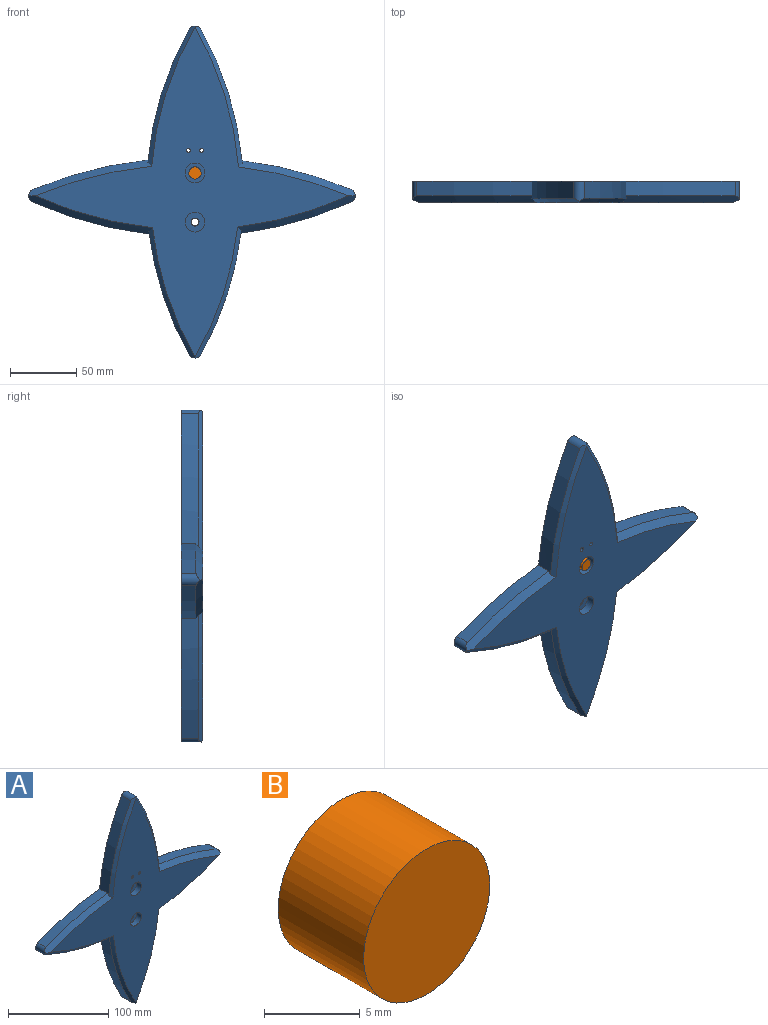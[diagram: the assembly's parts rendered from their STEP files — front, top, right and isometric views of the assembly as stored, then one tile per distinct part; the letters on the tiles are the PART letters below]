
ASSEMBLY  parts=2 mates=1
PART A: 30 faces, bbox 248.6x16x252.7 mm
  f0: cylinder r=3mm len=9.5mm, axis (0,1,0), area 179.1mm2, adj f10,f12
  f1: cylinder r=289.43mm len=87.94mm, axis (0,1,0), area 1007.8mm2, adj f2,f10,f18,f25
  f2: cylinder r=250mm len=92.9mm, axis (0,1,0), area 1254mm2, adj f1,f10,f18,f21,f23
  f3: cylinder r=250mm len=93.46mm, axis (0,1,0), area 1261.3mm2, adj f4,f10,f15,f22,f23
  f4: cylinder r=289.43mm len=83.32mm, axis (0,1,0), area 956.6mm2, adj f3,f10,f15,f26
  f5: cylinder r=310.23mm len=82.35mm, axis (0,1,0), area 940.1mm2, adj f6,f10,f16,f26
  f6: cylinder r=250mm len=100.98mm, axis (0,1,0), area 1359.7mm2, adj f5,f10,f16,f20,f24
  f7: cylinder r=250mm len=100.45mm, axis (0,1,0), area 1352.8mm2, adj f8,f10,f17,f19,f24
  f8: cylinder r=310.23mm len=86.95mm, axis (0,1,0), area 991.1mm2, adj f7,f10,f17,f25
  f9: plane 248.27x236.06mm, normal (0,-1,0), area 15523.8mm2, adj f11,f13,f15,f16,f17,f18,f19,f20
  f10: plane 250.21x246.06mm, normal (0,1,0), area 18914.9mm2, adj f0,f1,f2,f3,f4,f5,f6,f7
  f11: cylinder r=7.5mm len=15mm, axis (0,-1,0), area 306.3mm2, adj f9,f12
  f12: plane 15x15mm, normal (0,-1,0), area 148.4mm2, adj f0,f11
  f13: cylinder r=7.5mm len=15mm, axis (0,-1,0), area 306.3mm2, adj f9,f14
  f14: plane 15x15mm, normal (0,-1,0), area 146.5mm2, adj f13,f29
  f15: cone r=284.43mm half-angle=45deg, axis (0,1,0), area 632.2mm2, adj f3,f4,f9,f16,f22,f26
  f16: cone r=305.23mm half-angle=45deg, axis (0,1,0), area 622.6mm2, adj f5,f6,f9,f15,f20,f26
  f17: cone r=305.23mm half-angle=45deg, axis (0,1,0), area 655.4mm2, adj f7,f8,f9,f18,f19,f25
  f18: cone r=284.43mm half-angle=45deg, axis (0,1,0), area 665.1mm2, adj f1,f2,f9,f17,f21,f25
  f19: cone r=247mm half-angle=45deg, axis (0,1,0), area 465.8mm2, adj f7,f9,f17,f20,f24
  f20: cone r=247mm half-angle=45deg, axis (0,1,0), area 468mm2, adj f6,f9,f16,f19,f24
  f21: cone r=247mm half-angle=45deg, axis (0,1,0), area 433.6mm2, adj f2,f9,f18,f22,f23
  f22: cone r=247mm half-angle=45deg, axis (0,1,0), area 435.9mm2, adj f3,f9,f15,f21,f23
  f23: cylinder r=5mm len=15.51mm, axis (0,1,0), area 146.8mm2, adj f2,f3,f10,f21,f22
  f24: cylinder r=5mm len=15.51mm, axis (0,1,0), area 146.8mm2, adj f6,f7,f10,f19,f20
  f25: cylinder r=5mm len=13.96mm, axis (0,1,0), area 139.4mm2, adj f1,f8,f10,f17,f18
  f26: cylinder r=5mm len=13.96mm, axis (0,1,0), area 139.4mm2, adj f4,f5,f10,f15,f16
  f27: cylinder r=1.5mm len=16mm, axis (0,-1,0), area 150.8mm2, adj f9,f10
  f28: cylinder r=1.5mm len=16mm, axis (0,-1,0), area 150.8mm2, adj f9,f10
  f29: cylinder r=3.1mm len=9.5mm, axis (0,-1,0), area 185mm2, adj f10,f14
PART B: 3 faces, bbox 9.3x6.3x9.3 mm
  f0: cylinder r=4.65mm len=9.3mm, axis (0,1,0), area 184.1mm2, adj f1,f2
  f1: plane 9.3x9.3mm, normal (0,-1,0), area 67.9mm2, adj f0
  f2: plane 9.3x9.3mm, normal (0,1,0), area 67.9mm2, adj f0
PLACE A t=(-1.87,57.98,-145.63)mm
PLACE B t=(0.2,48.48,-128.63)mm
MATE fastened B.f0 <-> A.f13  axis (0,1,0) through (0.2,48.48,-128.63)mm
